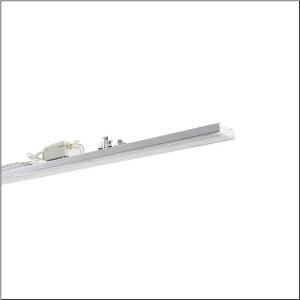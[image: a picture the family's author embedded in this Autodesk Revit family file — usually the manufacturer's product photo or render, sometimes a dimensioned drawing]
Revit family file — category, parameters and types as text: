
# Revit family: licross_21_recessed_ho_51te11vn4c5s
name_source: partatom
category: Lighting Fixtures
units: mm (PartAtom-declared; Revit-internal decimal feet)

## family parameters
Cut with Voids When Loaded = No
Host = Face
Light Source = No
Part Type = Normal
Room Calculation Point = No
Round Connector Dimension = Use Diameter
Shared = No

## types (1)
- --- (1 x LED, 12960 lm, 70.6 W, 4000K)
    Apparent Load = 71 VA
    CIE Flux Codes = 84 94 98 99 100
    Color Rendering = 80
    Color Temperature = 4000K
    Default Elevation = 1800 mm
    Description = Licross 21 Recessed HO, luminaire insert, of sheet steel, galvanised, coil coated, white, length: 1.500mm, width: 66mm, height: 67mm, LED rated luminous flux: 12.960lm, light colour: 840, SDCM (Standard Deviation of Colour Matching)MacAdam ≤ 2 SDCM (initial), control gear: DALI 2, CLO, with plug, 5-pole, with phase selection, mains connection: 220..240V, AC, 50/60Hz, start of lifetime: 71W, end of service life: 77W, internal wiring halogen-free, primary optical cover: cover, of PMMA, light emission: direct distribution, primary light characteristic: symmetric, protection rating (complete): IP54, insulation class (complete): insulation class I (protective earthing), certification: CE, ENEC, VDE, UKCA, protection symbol: D if used in an environment with non-conductive dust loads with corresponding accessories, impact resistance: IK06, permissible ambient temperature for indoor applications: -25..+35°C, corresponds to IFS (International Featured Standards) requirements for safety and quality in the food industry, reducing of maximum allowable ambient temperature of 5°C with ceiling mounting, LABS conformity tested according to VDMA 24364:2018-05, The light source and the operating device comply with the requirements of the Ecodesign Regulation (EU) 2019/2020 and are replaceable in accordance with this regulation, packaging unit: 1 piece
    Height = 58 mm
    Lamp = 1 x LED
    Lamp Light Flux = 12960 lm
    Lamp Power = 70.6 W
    Lamp count = 1
    Length = 1500 mm
    Luminous efficacy = 184 lm/W
    Manufacturer = Siteco
    ModVariant = No
    Model = 51TE11VN4C5S
    Mounting Place = Ceiling
    Mounting Type = Pendant
    Number of Poles = 1
    OnlyDefault = Yes
    Power Factor = 1
    Product Name = Licross 21 Recessed HO
    Product group = luminaire insert | ceiling pendant
    ProductGroupID = 901
    Protection Class = Protection class I
    Protection Degree = IP 54
    RLX_Detail_Level = 1
    RLX_Emergency_Light_Flux = 0 lm
    RLX_Emergency_Type = 0
    RLX_Emergency_Type_DB = No
    RlxData = <blob elided: 25201 chars, md5=86d7b2f2>
    Socket = socket
    Standby Power = 0 W
    System Light Flux = 12960 lm
    System Power = 71 W
    Type Comments = factory setting: luminous flux: 100 % | dim-lin: 254 | 480 mA
    Type Image = l_1296930.jpg
    URL = http://relux.com
    VarID = @adj_000773
    Voltage = 0 V
    Weight = 0.00 kg
    Width = 66 mm

## geometry (parser evidence)
native form markers: Blend x4, Sweep x10
no freeform markers — native parametric forms only
